# Revit family: PD3 AP types Sans hôte
name_source: partatom
category: Dispositifs d'éclairage
units: mm (PartAtom-declared; Revit-internal decimal feet)

## family parameters
Basée sur le plan de construction = Oui
Conserver l'orientation des annotations = Non
Cote de connecteur circulaire = Utiliser le diamètre
Couper avec des vides une fois chargée = Non
Partagée = Non
Point de calcul de pièce = Non
Toujours verticalement = Oui
Type d'élément = Normal

## types (4) — shared parameters
Alimentation = 110-240 V AC
Classe = II
Code d'assemblage = D5010200
Fabricant = B.E.G.
Hauteur de montage max = 300 cm
IP = 44
Image du type = 360°.jpg
Marque = LUXOMAT
Mode de pose = Saillie
Température ambiante = -25°C à +50°C
URL = http://www.luxomat.com
zero-valued in all types: Elévation par défaut

## per-type parameters (varying)
| type | Charge Cos ɸ =0.5 | Charge Cos ɸ =1 | Charge LED | Commentaires du type | Consommation | Modèle | Relais | Référence | Type de Sortie |
| 01- PD3 AP Générique |  |  |  | DET.MOUV.360°/Ø10M APPARENT |  | PD3 AP |  |  |  |
| 03- PD3N 1C MICRO AP réf 92219 | 1150 VA | 2300 W | 300 W | DET.MOUV.1 CONTACT + MICRO.360°/Ø10M APPARENT | 0,49 W | PD3N 1C MICRO AP | 10 A | 92219 | TOR |
| 04- PD3 1C AP réf 92194 | 1000 VA | 2000 W | 250 W | DET.MOUV.1 CONTACT.360°/Ø10M APPARENT NON TELECOMMANDABLE | < 1W | PD3 1C AP | 8,7 A | 92194 | TOR |
| 02- PD3N 1C AP réf 92190 | 1150 VA | 2300 W | 300 W | DET.MOUV.1 CONTACT.360°/Ø10M APPARENT | 0,25 W | PD3N 1C AP | 10 A | 92190 | TOR |
